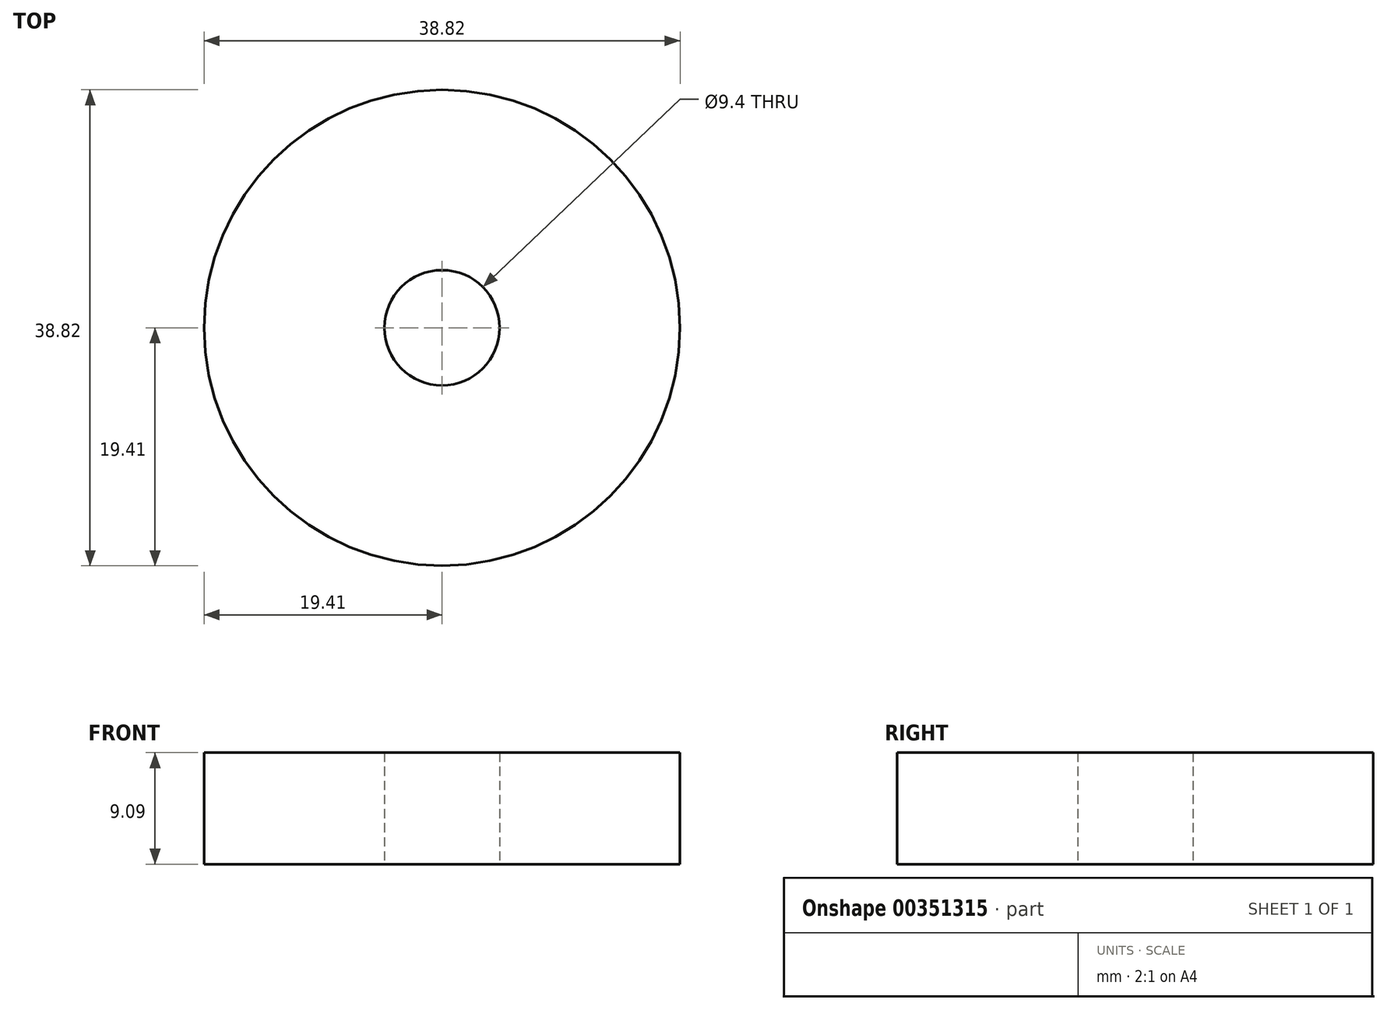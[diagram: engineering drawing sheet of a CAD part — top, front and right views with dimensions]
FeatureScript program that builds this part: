
annotation { "Feature Type Name" : "Feature", "Feature Type Description" : "" }
export const myFeature = defineFeature(function(context is Context, id is Id, definition is map)
    precondition{}
    {
        {
            var Q0;
            Q0=qCreatedBy(makeId("Top.planeOp"),FACE);
            var sketch = newSketch(context, id + "F0", { "sketchPlane" : qUnion([Q0])});
            skCircle(sketch, "E0", {"center": v(0, 0) * mm, "radius": 19.4 * mm});
            skCircle(sketch, "E1", {"center": v(0, 0) * mm, "radius": 4.7 * mm});
            skSolve(sketch);
        }
        {
            var Q0;
            Q0 = qSketchRegion(id + "F0", true);
            extrude(context, id + "F1", {"entities" : qUnion([Q0]), "depth" : 9.1 * mm});
        }
    });
